annotation { "Feature Type Name" : "Feature", "Feature Type Description" : "" }
export const myFeature = defineFeature(function(context is Context, id is Id, definition is map)
    precondition{}
    {
        {
            var Q0;
            Q0=qCreatedBy(makeId("Top.planeOp"),FACE);
            var sketch = newSketch(context, id + "F0", { "sketchPlane" : qUnion([Q0])});
            skLineSegment(sketch, "E0.bottom", {"start": v(0, 127) * mm, "end": v(-127, 127) * mm});
            skLineSegment(sketch, "E0.top", {"start": v(127, -127) * mm, "end": v(0, -127) * mm});
            skLineSegment(sketch, "E0.left", {"start": v(127, 0) * mm, "end": v(127, -127) * mm});
            skLineSegment(sketch, "E0.right", {"start": v(-127, 127) * mm, "end": v(-127, 0) * mm});
            skPoint(sketch, "E0.middle", {"position": v(0, 0) * mm});
            skLineSegment(sketch, "E1.bottom", {"start": v(228.6, 228.6) * mm, "end": v(-279.4, 228.6) * mm});
            skLineSegment(sketch, "E1.top", {"start": v(228.6, -228.6) * mm, "end": v(-279.4, -228.6) * mm});
            skLineSegment(sketch, "E1.right", {"start": v(-279.4, 228.6) * mm, "end": v(-279.4, -228.6) * mm});
            skLineSegment(sketch, "E2", {"start": v(228.6, 228.6) * mm, "end": v(228.6, -228.6) * mm});
            skLineSegment(sketch, "E3.bottom", {"start": v(0, 0) * mm, "end": v(-127, 0) * mm});
            skLineSegment(sketch, "E3.left", {"start": v(0, 0) * mm, "end": v(0, 127) * mm});
            skLineSegment(sketch, "E3.right", {"start": v(-127, 0) * mm, "end": v(-127, 127) * mm});
            skLineSegment(sketch, "E4.bottom", {"start": v(0, 0) * mm, "end": v(127, 0) * mm});
            skLineSegment(sketch, "E4.top", {"start": v(0, -127) * mm, "end": v(127, -127) * mm});
            skLineSegment(sketch, "E4.left", {"start": v(0, 0) * mm, "end": v(0, -127) * mm});
            skLineSegment(sketch, "E5", {"start": v(-127, 0) * mm, "end": v(-228.6, 0) * mm, "construction": true});
            skPoint(sketch, "E6.middle", {"position": v(-228.6, 0) * mm});
            skLineSegment(sketch, "E7.bottom", {"start": v(-222.25, 50.8) * mm, "end": v(-234.95, 50.8) * mm});
            skLineSegment(sketch, "E7.top", {"start": v(-222.25, -50.8) * mm, "end": v(-234.95, -50.8) * mm});
            skLineSegment(sketch, "E7.left", {"start": v(-209.55, 38.1) * mm, "end": v(-209.55, -38.1) * mm});
            skLineSegment(sketch, "E7.right", {"start": v(-247.65, 38.1) * mm, "end": v(-247.65, -38.1) * mm});
            skPoint(sketch, "E8.visualSharp", {"position": v(-247.65, 50.8) * mm});
            skArc(sketch, "E8.filletArc", {"start": v(-234.95, 50.8) * mm, "mid": v(-243.93, 47.08) * mm, "end": v(-247.65, 38.1) * mm});
            skPoint(sketch, "E9.visualSharp", {"position": v(-209.55, 50.8) * mm});
            skArc(sketch, "E9.filletArc", {"start": v(-209.55, 38.1) * mm, "mid": v(-213.27, 47.08) * mm, "end": v(-222.25, 50.8) * mm});
            skPoint(sketch, "E10.visualSharp", {"position": v(-247.65, -50.8) * mm});
            skArc(sketch, "E10.filletArc", {"start": v(-247.65, -38.1) * mm, "mid": v(-243.93, -47.08) * mm, "end": v(-234.95, -50.8) * mm});
            skPoint(sketch, "E11.visualSharp", {"position": v(-209.55, -50.8) * mm});
            skArc(sketch, "E11.filletArc", {"start": v(-222.25, -50.8) * mm, "mid": v(-213.27, -47.08) * mm, "end": v(-209.55, -38.1) * mm});
            skLineSegment(sketch, "E12.bottom", {"start": v(158.75, 158.75) * mm, "end": v(-158.75, 158.75) * mm, "construction": true});
            skLineSegment(sketch, "E12.top", {"start": v(158.75, -158.75) * mm, "end": v(-158.75, -158.75) * mm, "construction": true});
            skLineSegment(sketch, "E12.left", {"start": v(158.75, 158.75) * mm, "end": v(158.75, -158.75) * mm, "construction": true});
            skLineSegment(sketch, "E12.right", {"start": v(-158.75, 158.75) * mm, "end": v(-158.75, -158.75) * mm, "construction": true});
            skPoint(sketch, "E13.middle", {"position": v(-176.03, -125.86) * mm});
            skPoint(sketch, "E14.visualSharp", {"position": v(-195.08, -75.06) * mm});
            skPoint(sketch, "E15.visualSharp", {"position": v(-156.98, -75.06) * mm});
            skPoint(sketch, "E16.visualSharp", {"position": v(-195.08, -176.66) * mm});
            skPoint(sketch, "E17.visualSharp", {"position": v(-156.98, -176.66) * mm});
            skLineSegment(sketch, "E18.bottom", {"start": v(814.67, -448.5) * mm, "end": v(560.67, -448.5) * mm});
            skLineSegment(sketch, "E18.top", {"start": v(814.67, -702.5) * mm, "end": v(560.67, -702.5) * mm});
            skLineSegment(sketch, "E18.left", {"start": v(814.67, -448.5) * mm, "end": v(814.67, -702.5) * mm});
            skLineSegment(sketch, "E18.right", {"start": v(560.67, -448.5) * mm, "end": v(560.67, -702.5) * mm});
            skLineSegment(sketch, "E19.bottom", {"start": v(916.27, -346.9) * mm, "end": v(408.27, -346.9) * mm});
            skLineSegment(sketch, "E19.top", {"start": v(916.27, -804.1) * mm, "end": v(408.27, -804.1) * mm});
            skLineSegment(sketch, "E19.right", {"start": v(408.27, -346.9) * mm, "end": v(408.27, -804.1) * mm});
            skLineSegment(sketch, "E20", {"start": v(916.27, -346.9) * mm, "end": v(916.27, -804.1) * mm});
            skLineSegment(sketch, "E21.right", {"start": v(560.67, -575.5) * mm, "end": v(560.67, -448.5) * mm});
            skPoint(sketch, "E22.middle", {"position": v(459.07, -575.5) * mm});
            skLineSegment(sketch, "E23.bottom", {"start": v(465.42, -524.7) * mm, "end": v(452.72, -524.7) * mm});
            skLineSegment(sketch, "E23.top", {"start": v(465.42, -626.3) * mm, "end": v(452.72, -626.3) * mm});
            skLineSegment(sketch, "E23.left", {"start": v(478.12, -537.4) * mm, "end": v(478.12, -613.6) * mm});
            skLineSegment(sketch, "E23.right", {"start": v(440.02, -537.4) * mm, "end": v(440.02, -613.6) * mm});
            skPoint(sketch, "E24.visualSharp", {"position": v(440.02, -524.7) * mm});
            skArc(sketch, "E24.filletArc", {"start": v(452.72, -524.7) * mm, "mid": v(443.74, -528.42) * mm, "end": v(440.02, -537.4) * mm});
            skPoint(sketch, "E25.visualSharp", {"position": v(478.12, -524.7) * mm});
            skArc(sketch, "E25.filletArc", {"start": v(478.12, -537.4) * mm, "mid": v(474.4, -528.42) * mm, "end": v(465.42, -524.7) * mm});
            skPoint(sketch, "E26.visualSharp", {"position": v(440.02, -626.3) * mm});
            skArc(sketch, "E26.filletArc", {"start": v(440.02, -613.6) * mm, "mid": v(443.74, -622.58) * mm, "end": v(452.72, -626.3) * mm});
            skPoint(sketch, "E27.visualSharp", {"position": v(478.12, -626.3) * mm});
            skArc(sketch, "E27.filletArc", {"start": v(465.42, -626.3) * mm, "mid": v(474.4, -622.58) * mm, "end": v(478.12, -613.6) * mm});
            skPoint(sketch, "E28.orphan", {"position": v(127, 127) * mm});
            skPoint(sketch, "E29.orphan", {"position": v(-127, -127) * mm});
            skSolve(sketch);
        }
        {
            var Q0;
            Q0=qCreatedBy(makeId("Top.planeOp"),FACE);
            var sketch = newSketch(context, id + "F1", { "sketchPlane" : qUnion([Q0])});
            skLineSegment(sketch, "E30", {"start": v(116.93, -327.85) * mm, "end": v(116.93, -0.02) * mm, "construction": true});
            skLineSegment(sketch, "E31.bottom", {"start": v(116.93, -327.85) * mm, "end": v(-391.07, -327.85) * mm});
            skLineSegment(sketch, "E31.top", {"start": v(116.93, -581.85) * mm, "end": v(-391.07, -581.85) * mm});
            skLineSegment(sketch, "E31.left", {"start": v(116.93, -327.85) * mm, "end": v(116.93, -581.85) * mm});
            skLineSegment(sketch, "E31.right", {"start": v(-391.07, -327.85) * mm, "end": v(-391.07, -581.85) * mm});
            skText(sketch, "E32", { "text": "SURVEY MONUMENT\n     DO NOT MOVE", "fontName": "AllertaStencil-Regular.ttf"});
            skLineSegment(sketch, "E33.bottom", {"start": v(-175.17, -563.79) * mm, "end": v(-98.97, -563.79) * mm});
            skLineSegment(sketch, "E33.top", {"start": v(-175.17, -525.69) * mm, "end": v(-98.97, -525.69) * mm});
            skLineSegment(sketch, "E33.left", {"start": v(-187.87, -551.09) * mm, "end": v(-187.87, -538.39) * mm});
            skLineSegment(sketch, "E33.right", {"start": v(-86.27, -551.09) * mm, "end": v(-86.27, -538.39) * mm});
            skPoint(sketch, "E34.visualSharp", {"position": v(-86.27, -525.69) * mm});
            skArc(sketch, "E34.filletArc", {"start": v(-86.27, -538.39) * mm, "mid": v(-89.99, -529.4) * mm, "end": v(-98.97, -525.69) * mm});
            skPoint(sketch, "E35.visualSharp", {"position": v(-86.27, -563.79) * mm});
            skArc(sketch, "E35.filletArc", {"start": v(-98.97, -563.79) * mm, "mid": v(-89.99, -560.07) * mm, "end": v(-86.27, -551.09) * mm});
            skPoint(sketch, "E36.visualSharp", {"position": v(-187.87, -563.79) * mm});
            skArc(sketch, "E36.filletArc", {"start": v(-187.87, -551.09) * mm, "mid": v(-184.15, -560.07) * mm, "end": v(-175.17, -563.79) * mm});
            skPoint(sketch, "E37.visualSharp", {"position": v(-187.87, -525.69) * mm});
            skArc(sketch, "E37.filletArc", {"start": v(-175.17, -525.69) * mm, "mid": v(-184.15, -529.4) * mm, "end": v(-187.87, -538.39) * mm});
            skLineSegment(sketch, "E38", {"start": v(-137.07, -327.85) * mm, "end": v(-137.07, -525.69) * mm});
            const initialGuessF1  = {"E32": [0.0571, -0.43268, -1, 0, 0.02783]};
            skSetInitialGuess(sketch, initialGuessF1);
            skSolve(sketch);
        }
        {
            var Q0;
            Q0=makeQuery(id+"F1.imprint","IMPRINT",FACE,{"disambiguationData":[TD([[makeQuery(id+"F1.imprint","IMPRINT",EDGE,{"derivedFrom":sQuery(id+"F1.wireOp",EDGE,"E31.bottom")}),1.0]])]});
            extrude(context, id + "F2", {"entities" : qUnion([Q0]), "depth" : 1.59 * mm, "offsetDistance" : 25.4 * mm});
        }
        {
            var Q0;
            Q0=makeQuery(id+"F0.imprint","IMPRINT",FACE,{"disambiguationData":[TD([[makeQuery(id+"F0.imprint","IMPRINT",EDGE,{"derivedFrom":sQuery(id+"F0.wireOp",EDGE,"E18.bottom")}),-1.0]])]});
            extrude(context, id + "F3", {"entities" : qUnion([Q0]), "depth" : 1.59 * mm, "offsetDistance" : 25.4 * mm});
        }
        {
            var Q0;
            Q0=qCreatedBy(makeId("Top.planeOp"),FACE);
            var sketch = newSketch(context, id + "F4", { "sketchPlane" : qUnion([Q0])});
            skLineSegment(sketch, "E39.bottom", {"start": v(283.62, 321.4) * mm, "end": v(791.62, 321.4) * mm});
            skLineSegment(sketch, "E39.top", {"start": v(283.62, -135.8) * mm, "end": v(791.62, -135.8) * mm});
            skLineSegment(sketch, "E39.left", {"start": v(283.62, 321.4) * mm, "end": v(283.62, -135.8) * mm});
            skLineSegment(sketch, "E39.right", {"start": v(791.62, 321.4) * mm, "end": v(791.62, -135.8) * mm});
            skLineSegment(sketch, "E40.bottom", {"start": v(336.65, 152.13) * mm, "end": v(323.95, 152.13) * mm});
            skLineSegment(sketch, "E40.top", {"start": v(336.65, 50.53) * mm, "end": v(323.95, 50.53) * mm});
            skLineSegment(sketch, "E40.left", {"start": v(349.35, 139.43) * mm, "end": v(349.35, 63.23) * mm});
            skLineSegment(sketch, "E40.right", {"start": v(311.25, 139.43) * mm, "end": v(311.25, 63.23) * mm});
            skPoint(sketch, "E40.middle", {"position": v(330.3, 101.33) * mm});
            skPoint(sketch, "E41.visualSharp", {"position": v(311.25, 152.13) * mm});
            skArc(sketch, "E41.filletArc", {"start": v(323.95, 152.13) * mm, "mid": v(314.97, 148.41) * mm, "end": v(311.25, 139.43) * mm});
            skPoint(sketch, "E42.visualSharp", {"position": v(349.35, 152.13) * mm});
            skArc(sketch, "E42.filletArc", {"start": v(349.35, 139.43) * mm, "mid": v(345.63, 148.41) * mm, "end": v(336.65, 152.13) * mm});
            skPoint(sketch, "E43.visualSharp", {"position": v(311.25, 50.53) * mm});
            skArc(sketch, "E43.filletArc", {"start": v(311.25, 63.23) * mm, "mid": v(314.97, 54.25) * mm, "end": v(323.95, 50.53) * mm});
            skPoint(sketch, "E44.visualSharp", {"position": v(349.35, 50.53) * mm});
            skArc(sketch, "E44.filletArc", {"start": v(336.65, 50.53) * mm, "mid": v(345.63, 54.25) * mm, "end": v(349.35, 63.23) * mm});
            skCircle(sketch, "E45", {"center": v(537.62, 92.8) * mm, "radius": 25.4 * mm});
            skPoint(sketch, "E45.centerSnap0", {"position": v(537.62, 321.4) * mm});
            skPoint(sketch, "E45.centerSnap1", {"position": v(791.62, 92.8) * mm});
            skSolve(sketch);
        }
        {
            var Q0;
            Q0=qCreatedBy(makeId("Top.planeOp"),FACE);
            var sketch = newSketch(context, id + "F5", { "sketchPlane" : qUnion([Q0])});
            skLineSegment(sketch, "E46.bottom", {"start": v(-132.86, 225) * mm, "end": v(-259.86, 225) * mm});
            skLineSegment(sketch, "E46.top", {"start": v(-5.86, -29) * mm, "end": v(-132.86, -29) * mm});
            skLineSegment(sketch, "E46.left", {"start": v(-5.86, 98) * mm, "end": v(-5.86, -29) * mm});
            skLineSegment(sketch, "E46.right", {"start": v(-259.86, 225) * mm, "end": v(-259.86, 98) * mm});
            skLineSegment(sketch, "E47.bottom", {"start": v(95.74, 326.6) * mm, "end": v(-412.26, 326.6) * mm});
            skLineSegment(sketch, "E47.top", {"start": v(95.74, -130.6) * mm, "end": v(-412.26, -130.6) * mm});
            skLineSegment(sketch, "E47.right", {"start": v(-412.26, 326.6) * mm, "end": v(-412.26, -130.6) * mm});
            skLineSegment(sketch, "E48", {"start": v(95.74, 326.6) * mm, "end": v(95.74, -130.6) * mm});
            skLineSegment(sketch, "E49.bottom", {"start": v(-132.86, 98) * mm, "end": v(-259.86, 98) * mm});
            skLineSegment(sketch, "E49.left", {"start": v(-132.86, 98) * mm, "end": v(-132.86, 225) * mm});
            skLineSegment(sketch, "E49.right", {"start": v(-259.86, 98) * mm, "end": v(-259.86, 225) * mm});
            skLineSegment(sketch, "E50.bottom", {"start": v(-132.86, 98) * mm, "end": v(-5.86, 98) * mm});
            skLineSegment(sketch, "E50.top", {"start": v(-132.86, -29) * mm, "end": v(-5.86, -29) * mm});
            skLineSegment(sketch, "E50.left", {"start": v(-132.86, 98) * mm, "end": v(-132.86, -29) * mm});
            skLineSegment(sketch, "E51.bottom", {"start": v(-355.1, 148.8) * mm, "end": v(-367.8, 148.8) * mm});
            skLineSegment(sketch, "E51.top", {"start": v(-355.1, 47.2) * mm, "end": v(-367.8, 47.2) * mm});
            skLineSegment(sketch, "E51.left", {"start": v(-342.4, 136.1) * mm, "end": v(-342.4, 59.9) * mm});
            skLineSegment(sketch, "E51.right", {"start": v(-380.5, 136.1) * mm, "end": v(-380.5, 59.9) * mm});
            skPoint(sketch, "E51.middle", {"position": v(-361.46, 98) * mm});
            skPoint(sketch, "E52.visualSharp", {"position": v(-380.5, 148.8) * mm});
            skArc(sketch, "E52.filletArc", {"start": v(-367.8, 148.8) * mm, "mid": v(-376.79, 145.09) * mm, "end": v(-380.5, 136.1) * mm});
            skPoint(sketch, "E53.visualSharp", {"position": v(-342.4, 148.8) * mm});
            skArc(sketch, "E53.filletArc", {"start": v(-342.4, 136.1) * mm, "mid": v(-346.13, 145.09) * mm, "end": v(-355.1, 148.8) * mm});
            skPoint(sketch, "E54.visualSharp", {"position": v(-380.5, 47.2) * mm});
            skArc(sketch, "E54.filletArc", {"start": v(-380.5, 59.9) * mm, "mid": v(-376.79, 50.93) * mm, "end": v(-367.8, 47.2) * mm});
            skPoint(sketch, "E55.visualSharp", {"position": v(-342.4, 47.2) * mm});
            skArc(sketch, "E55.filletArc", {"start": v(-355.1, 47.2) * mm, "mid": v(-346.13, 50.93) * mm, "end": v(-342.4, 59.9) * mm});
            skPoint(sketch, "E56.middle", {"position": v(-132.86, 98) * mm});
            skCircle(sketch, "E57", {"center": v(-132.86, 98) * mm, "radius": 6.35 * mm});
            skSolve(sketch);
        }
        {
            var Q0;
            Q0=makeQuery(id+"F5.imprint","IMPRINT",FACE,{"disambiguationData":[TD([[makeQuery(id+"F5.imprint","IMPRINT",EDGE,{"derivedFrom":sQuery(id+"F5.wireOp",EDGE,"E47.bottom")}),1.0]])]});
            extrude(context, id + "F6", {"entities" : qUnion([Q0]), "oppositeDirection" : true, "depth" : 1.59 * mm, "offsetDistance" : 25.4 * mm});
        }
        {
            var Q0;
            Q0=makeQuery(id+"F4.imprint","IMPRINT",FACE,{"disambiguationData":[TD([[makeQuery(id+"F4.imprint","IMPRINT",EDGE,{"derivedFrom":sQuery(id+"F4.wireOp",EDGE,"E39.bottom")}),-1.0]])]});
            extrude(context, id + "F7", {"entities" : qUnion([Q0]), "depth" : 1.59 * mm, "offsetDistance" : 25.4 * mm});
        }
    });